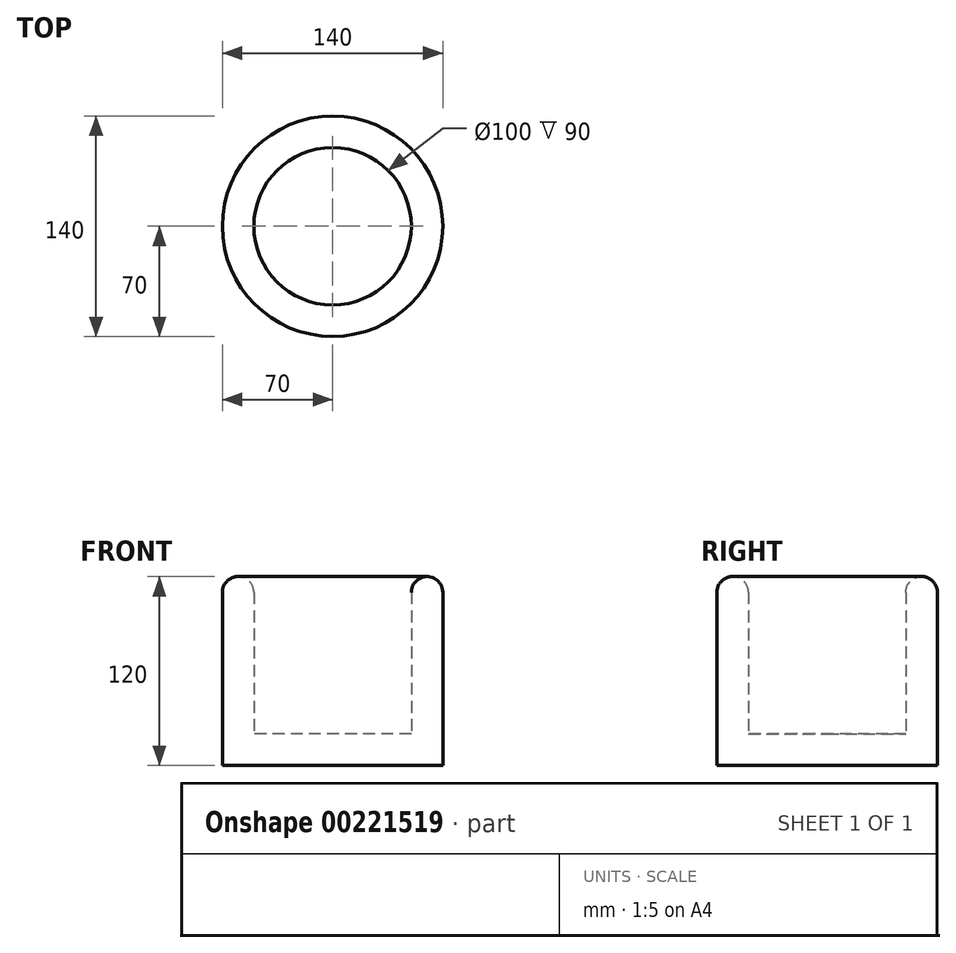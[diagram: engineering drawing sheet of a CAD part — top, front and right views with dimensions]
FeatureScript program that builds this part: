
annotation { "Feature Type Name" : "Feature", "Feature Type Description" : "" }
export const myFeature = defineFeature(function(context is Context, id is Id, definition is map)
    precondition{}
    {
        {
            assignVariable(context, id + "F0", {"name" : "insulation_thickness", "anyValue" : 20});
        }
        {
            assignVariable(context, id + "F1", {"name" : "cooler_depth", "anyValue" : 100});
        }
        {
            var Q0;
            Q0=qCreatedBy(makeId("Top.planeOp"),FACE);
            var sketch = newSketch(context, id + "F2", { "sketchPlane" : qUnion([Q0])});
            skCircle(sketch, "E0", {"center": v(0, 0) * mm, "radius": 70 * mm});
            skSolve(sketch);
        }
        {
            var Q0;
            Q0=makeQuery(id+"F2.imprint","IMPRINT",FACE,{"disambiguationData":[TD([[makeQuery(id+"F2.imprint","IMPRINT",EDGE,{"derivedFrom":sQuery(id+"F2.wireOp",EDGE,"E0")}),1.0]])]});
            extrude(context, id + "F3", {"entities" : qUnion([Q0]), "depth" : (getVariable(context, 'insulation_thickness')) * mm});
        }
        {
            var Q0;
            Q0=makeQuery(id+"F3.opExtrude","CAP_FACE",FACE,{"disambiguationData":[OSD([sQuery(id+"F2.wireOp",EDGE,"E0")])],"isStart":false});
            var sketch = newSketch(context, id + "F4", { "sketchPlane" : qUnion([Q0])});
            skCircle(sketch, "E1", {"center": v(0, 0) * mm, "radius": 50 * mm});
            skSolve(sketch);
        }
        {
            var Q0;
            Q0=makeQuery(id+"F4.imprint","IMPRINT",FACE,{"disambiguationData":[TD([[makeQuery(id+"F4.imprint","IMPRINT",EDGE,{"derivedFrom":sQuery(id+"F4.wireOp",EDGE,"E1")}),-1.0]])]});
            extrude(context, id + "F5", {"entities" : qUnion([Q0]), "operationType" : NewBodyOperationType.ADD, "depth" : (getVariable(context, 'cooler_depth')) * mm});
        }
        {
            var Q0;
            Q0=makeQuery(id+"F5.opExtrude","CAP_EDGE",EDGE,{"disambiguationData":[OSD([sQuery(id+"F4.wireOp",EDGE,"E1")])],"isStart":false});
            var Q1;
            Q1=makeQuery(id+"F5.opExtrude","CAP_EDGE",EDGE,{"disambiguationData":[OSD([sQuery(id+"F2.wireOp",EDGE,"E0")])],"isStart":false});
            fillet(context, id + "F6", {"entities" : qUnion([Q0, Q1]), "radius" : (getVariable(context, 'insulation_thickness') / 2) * mm, "tangentPropagation" : true, "allowEdgeOverflow" : false});
        }
    });
